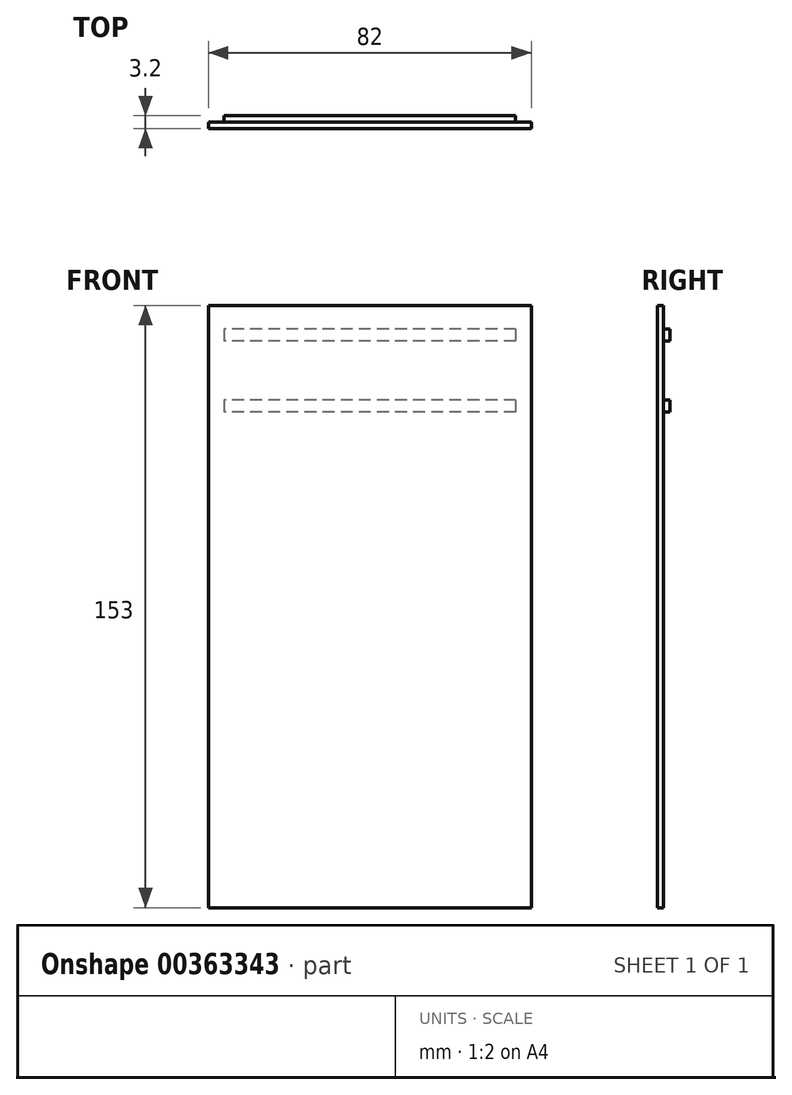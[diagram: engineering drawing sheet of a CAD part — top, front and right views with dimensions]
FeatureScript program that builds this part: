
annotation { "Feature Type Name" : "Feature", "Feature Type Description" : "" }
export const myFeature = defineFeature(function(context is Context, id is Id, definition is map)
    precondition{}
    {
        {
            var Q0;
            Q0=qCreatedBy(makeId("Front.planeOp"),FACE);
            var sketch = newSketch(context, id + "F0", { "sketchPlane" : qUnion([Q0])});
            skLineSegment(sketch, "E0", {"start": v(-82, 76.5) * mm, "end": v(0, 76.5) * mm});
            skLineSegment(sketch, "E1", {"start": v(0, 76.5) * mm, "end": v(0, -76.5) * mm});
            skLineSegment(sketch, "E2", {"start": v(0, -76.5) * mm, "end": v(-82, -76.5) * mm});
            skLineSegment(sketch, "E3", {"start": v(-82, -76.5) * mm, "end": v(-82, 76.5) * mm});
            skSolve(sketch);
        }
        {
            var Q0;
            Q0=qSketchRegion(id+"F0",true);
            extrude(context, id + "F1", {"entities" : qUnion([Q0]), "depth" : 1.6 * mm});
        }
        {
            var Q0;
            Q0=qCreatedBy(makeId("Front.planeOp"),FACE);
            var sketch = newSketch(context, id + "F2", { "sketchPlane" : qUnion([Q0])});
            skLineSegment(sketch, "E4", {"start": v(-4, 70.5) * mm, "end": v(-78, 70.5) * mm});
            skLineSegment(sketch, "E5", {"start": v(-78, 70.5) * mm, "end": v(-78, 67.5) * mm});
            skLineSegment(sketch, "E6", {"start": v(-4, 70.5) * mm, "end": v(-4, 67.5) * mm});
            skLineSegment(sketch, "E7", {"start": v(-4, 67.5) * mm, "end": v(-78, 67.5) * mm});
            skLineSegment(sketch, "E8", {"start": v(-4, 52.5) * mm, "end": v(-78, 52.5) * mm});
            skLineSegment(sketch, "E9", {"start": v(-78, 52.5) * mm, "end": v(-78, 49.5) * mm});
            skLineSegment(sketch, "E10", {"start": v(-4, 52.5) * mm, "end": v(-4, 49.5) * mm});
            skLineSegment(sketch, "E11", {"start": v(-4, 49.5) * mm, "end": v(-78, 49.5) * mm});
            skSolve(sketch);
        }
        {
            var Q0;
            Q0 = qSketchRegion(id + "F2", true);
            extrude(context, id + "F3", {"entities" : qUnion([Q0]), "operationType" : NewBodyOperationType.ADD, "oppositeDirection" : true, "depth" : 1.6 * mm});
        }
    });
